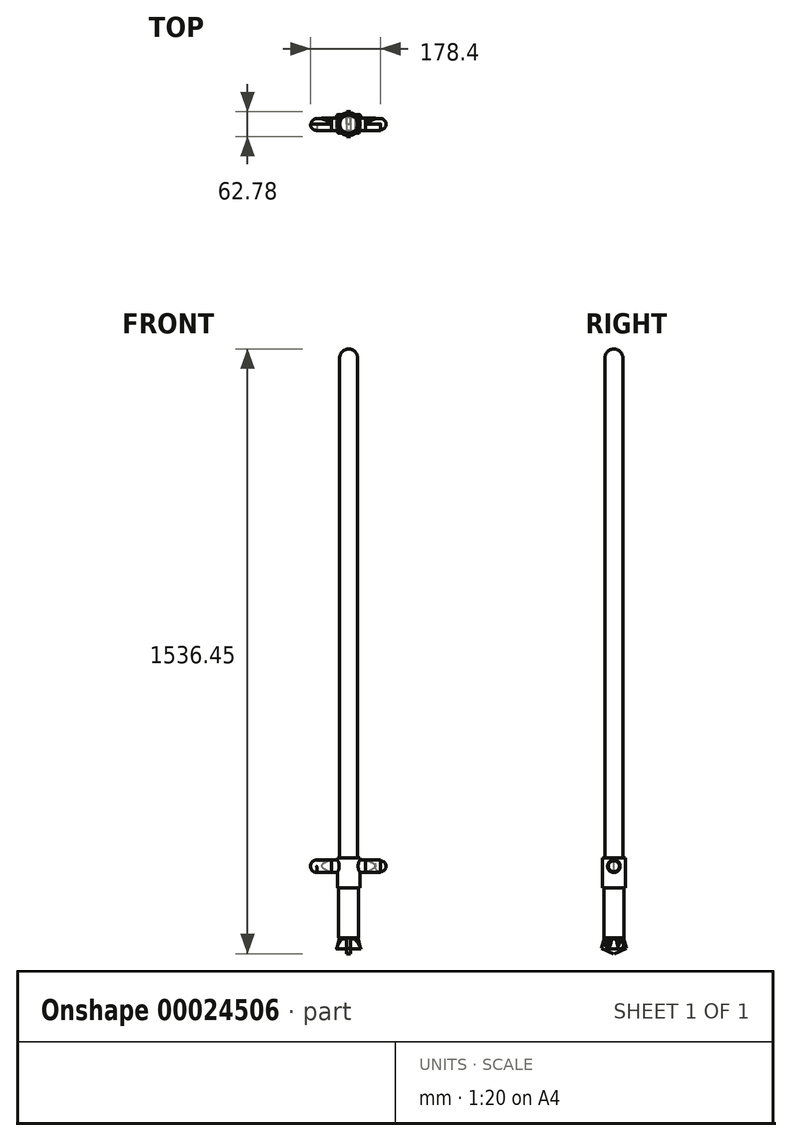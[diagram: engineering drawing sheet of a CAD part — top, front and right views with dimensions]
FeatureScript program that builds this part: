
annotation { "Feature Type Name" : "Feature", "Feature Type Description" : "" }
export const myFeature = defineFeature(function(context is Context, id is Id, definition is map)
    precondition{}
    {
        {
            var Q0;
            Q0=qCreatedBy(makeId("Top.planeOp"),FACE);
            var sketch = newSketch(context, id + "F0", { "sketchPlane" : qUnion([Q0])});
            skCircle(sketch, "E0", {"center": v(0, 0) * mm, "radius": 25.4 * mm});
            skSolve(sketch);
        }
        {
            var Q0;
            Q0 = qSketchRegion(id + "F0", true);
            extrude(context, id + "F1", {"entities" : qUnion([Q0]), "depth" : 152.4 * mm});
        }
        {
            var Q0;
            Q0=qCreatedBy(makeId("Right.planeOp"),FACE);
            var sketch = newSketch(context, id + "F2", { "sketchPlane" : qUnion([Q0])});
            skCircle(sketch, "E1", {"center": v(0, 131.2) * mm, "radius": 15.84 * mm});
            skSolve(sketch);
        }
        {
            var Q0;
            Q0 = qSketchRegion(id + "F2", true);
            extrude(context, id + "F3", {"entities" : qUnion([Q0]), "operationType" : NewBodyOperationType.ADD, "depth" : 43.18 * mm, "hasSecondDirection" : true, "secondDirectionOppositeDirection" : true, "secondDirectionDepth" : 43.18 * mm});
        }
        {
            var Q0;
            Q0=makeQuery(id+"F3.opExtrude","CAP_FACE",FACE,{"disambiguationData":[OSD([sQuery(id+"F2.wireOp",EDGE,"E1")])],"isStart":true});
            var sketch = newSketch(context, id + "F4", { "sketchPlane" : qUnion([Q0])});
            skArc(sketch, "E2", {"start": v(0, 147.04) * mm, "mid": v(-15.79, 131.2) * mm, "end": v(0, 115.37) * mm});
            skLineSegment(sketch, "E3", {"start": v(0, 147.04) * mm, "end": v(0, 145.08) * mm});
            skLineSegment(sketch, "E4", {"start": v(0, 115.37) * mm, "end": v(0, 117.32) * mm});
            skArc(sketch, "E5", {"start": v(0, 145.08) * mm, "mid": v(-14.08, 131.2) * mm, "end": v(0, 117.32) * mm});
            skSolve(sketch);
        }
        {
            var Q0;
            Q0 = qSketchRegion(id + "F4", true);
            extrude(context, id + "F5", {"entities" : qUnion([Q0]), "operationType" : NewBodyOperationType.ADD, "depth" : 25.4 * mm});
        }
        {
            var Q0;
            Q0=qCreatedBy(makeId("Front.planeOp"),FACE);
            cPlane(context, id + "F6", {"entities" : qUnion([Q0]), "cplaneType" : CPlaneType.OFFSET, "offset" : 25.4 * mm, "width" : 152.4 * mm, "height" : 152.4 * mm});
        }
        {
            var Q0;
            Q0=qCreatedBy(id+"F6.planeOp",FACE);
            var sketch = newSketch(context, id + "F7", { "sketchPlane" : qUnion([Q0])});
            skFitSpline(sketch, "E6", {"points": [v(-43.17, 147.15) * mm, v(-68.76, 132.35) * mm, v(-43.02, 115.24) * mm], "startDerivative": vector(-77.14, -28.96) * mm, "endDerivative": vector(76.87, -34.83) * mm});
            skLineSegment(sketch, "E7", {"start": v(-43.17, 147.15) * mm, "end": v(-43.17, 153) * mm});
            skLineSegment(sketch, "E8", {"start": v(-43.02, 115.24) * mm, "end": v(-43.02, 106.3) * mm});
            skLineSegment(sketch, "E9", {"start": v(-43.02, 106.3) * mm, "end": v(-74.3, 104.91) * mm});
            skLineSegment(sketch, "E10", {"start": v(-74.3, 104.91) * mm, "end": v(-72, 148.07) * mm});
            skLineSegment(sketch, "E11", {"start": v(-72, 148.07) * mm, "end": v(-43.17, 153) * mm});
            skSolve(sketch);
        }
        {
            var Q0;
            Q0 = qSketchRegion(id + "F7", true);
            extrude(context, id + "F8", {"entities" : qUnion([Q0]), "operationType" : NewBodyOperationType.REMOVE, "oppositeDirection" : true, "depth" : 50.68 * mm});
        }
        {
            var Q0;
            Q0=makeQuery(id+"F1.opExtrude","SWEPT_BODY",BODY,{"disambiguationData":[OSD([sQuery(id+"F0.wireOp",EDGE,"E0")])]});
            var Q1;
            Q1=qCreatedBy(makeId("Right.planeOp"),FACE);
            mirror(context, id + "F9", {"entities" : qUnion([Q0]), "mirrorPlane" : qUnion([Q1])});
        }
        {
            var Q0;
            Q0=makeQuery(id+"F1.opExtrude","CAP_FACE",FACE,{"disambiguationData":[OSD([sQuery(id+"F0.wireOp",EDGE,"E0")])],"isStart":false});
            var sketch = newSketch(context, id + "F10", { "sketchPlane" : qUnion([Q0])});
            skCircle(sketch, "E12", {"center": v(0, 0) * mm, "radius": 28.73 * mm});
            skSolve(sketch);
        }
        {
            var Q0;
            Q0=makeQuery(id+"F10.imprint","IMPRINT",FACE,{"disambiguationData":[TD([[makeQuery(id+"F10.imprint","IMPRINT",EDGE,{"derivedFrom":sQuery(id+"F10.wireOp",EDGE,"E12")}),1.0]])]});
            extrude(context, id + "F11", {"entities" : qUnion([Q0]), "operationType" : NewBodyOperationType.ADD, "oppositeDirection" : true, "depth" : 76.2 * mm});
        }
        {
            var Q0;
            Q0=makeQuery(id+"F1.opExtrude","CAP_FACE",FACE,{"disambiguationData":[OSD([sQuery(id+"F0.wireOp",EDGE,"E0")])],"isStart":true});
            extrude(context, id + "F12", {"entities" : qUnion([Q0]), "operationType" : NewBodyOperationType.ADD, "depth" : 50.8 * mm});
        }
        {
            var Q0;
            Q0=makeQuery(id+"F12.opExtrude","CAP_FACE",FACE,{"disambiguationData":[OSD([sQuery(id+"F0.wireOp",EDGE,"E0")])],"isStart":false});
            var sketch = newSketch(context, id + "F13", { "sketchPlane" : qUnion([Q0])});
            skLineSegment(sketch, "E13.bottom", {"start": v(-18.87, 17) * mm, "end": v(17.98, 17) * mm});
            skLineSegment(sketch, "E13.top", {"start": v(-18.87, -17.94) * mm, "end": v(17.98, -17.94) * mm});
            skLineSegment(sketch, "E13.left", {"start": v(-18.87, 17) * mm, "end": v(-18.87, -17.94) * mm});
            skLineSegment(sketch, "E13.right", {"start": v(17.98, 17) * mm, "end": v(17.98, -17.94) * mm});
            skSolve(sketch);
        }
        {
            var Q0;
            Q0 = qSketchRegion(id + "F13", true);
            extrude(context, id + "F14", {"entities" : qUnion([Q0]), "operationType" : NewBodyOperationType.ADD, "depth" : 2.54 * mm});
        }
        {
            var Q0;
            Q0=makeQuery(id+"F14.opExtrude","CAP_FACE",FACE,{"disambiguationData":[OSD([sQuery(id+"F13.wireOp",EDGE,"E13.bottom"),sQuery(id+"F13.wireOp",EDGE,"E13.top"),sQuery(id+"F13.wireOp",EDGE,"E13.left"),sQuery(id+"F13.wireOp",EDGE,"E13.right")])],"isStart":false});
            cPlane(context, id + "F15", {"entities" : qUnion([Q0]), "cplaneType" : CPlaneType.OFFSET, "offset" : 25.4 * mm, "width" : 152.4 * mm, "height" : 152.4 * mm});
        }
        {
            var Q0;
            Q0=qCreatedBy(id+"F15.planeOp",FACE);
            var sketch = newSketch(context, id + "F16", { "sketchPlane" : qUnion([Q0])});
            skLineSegment(sketch, "E14.bottom", {"start": v(-31.75, 31.75) * mm, "end": v(31.75, 31.75) * mm});
            skLineSegment(sketch, "E14.top", {"start": v(-31.75, -31.75) * mm, "end": v(31.75, -31.75) * mm});
            skLineSegment(sketch, "E14.left", {"start": v(-31.75, 31.75) * mm, "end": v(-31.75, -31.75) * mm});
            skLineSegment(sketch, "E14.right", {"start": v(31.75, 31.75) * mm, "end": v(31.75, -31.75) * mm});
            skSolve(sketch);
        }
        {
            var Q1;
            Q1=makeQuery(id+"F14.opExtrude","CAP_FACE",FACE,{"disambiguationData":[OSD([sQuery(id+"F13.wireOp",EDGE,"E13.bottom"),sQuery(id+"F13.wireOp",EDGE,"E13.top"),sQuery(id+"F13.wireOp",EDGE,"E13.left"),sQuery(id+"F13.wireOp",EDGE,"E13.right")])],"isStart":false});
            var Q2;
            Q2=makeQuery(id+"F16.imprint","IMPRINT",FACE,{"disambiguationData":[TD([[makeQuery(id+"F16.imprint","IMPRINT",EDGE,{"derivedFrom":sQuery(id+"F16.wireOp",EDGE,"E14.bottom")}),-1.0]])]});
            loft(context, id + "F17", {"operationType" : NewBodyOperationType.ADD, "sheetProfilesArray" : [{ "sheetProfileEntities" : qUnion([Q1]) }, { "sheetProfileEntities" : qUnion([Q2]) }]});
        }
        {
            var Q0;
            Q0=makeQuery(id+"F17.opLoft","CAP_FACE",FACE,{"disambiguationData":[OSD([makeQuery(id+"F16.imprint","IMPRINT",FACE,{"disambiguationData":[TD([[makeQuery(id+"F16.imprint","IMPRINT",EDGE,{"derivedFrom":sQuery(id+"F16.wireOp",EDGE,"E14.bottom")}),-1.0]])]})])],"isStart":true});
            var sketch = newSketch(context, id + "F18", { "sketchPlane" : qUnion([Q0])});
            skCircle(sketch, "E15", {"center": v(0, 0) * mm, "radius": 23.24 * mm});
            skSolve(sketch);
        }
        {
            var Q0;
            Q0=qCreatedBy(makeId("Right.planeOp"),FACE);
            var sketch = newSketch(context, id + "F19", { "sketchPlane" : qUnion([Q0])});
            skLineSegment(sketch, "E16", {"start": v(-15.1, -41.8) * mm, "end": v(-31.4, -77.47) * mm});
            skLineSegment(sketch, "E17", {"start": v(-15.1, -41.8) * mm, "end": v(-21, -39.1) * mm});
            skLineSegment(sketch, "E18", {"start": v(-21, -39.1) * mm, "end": v(-31.4, -77.47) * mm});
            skSolve(sketch);
        }
        {
            var Q0;
            Q0 = qSketchRegion(id + "F19", true);
            extrude(context, id + "F20", {"entities" : qUnion([Q0]), "depth" : 5.08 * mm, "hasSecondDirection" : true, "secondDirectionOppositeDirection" : true, "secondDirectionDepth" : 5.08 * mm});
        }
        {
            var Q0;
            Q0=makeQuery(id+"F20.opExtrude","SWEPT_BODY",BODY,{"disambiguationData":[OSD([sQuery(id+"F19.wireOp",EDGE,"E16"),sQuery(id+"F19.wireOp",EDGE,"E17"),sQuery(id+"F19.wireOp",EDGE,"E18")])]});
            var Q1;
            Q1=sQuery(id+"F18.wireOp",EDGE,"E15");
            circularPattern(context, id + "F21", {"operationType" : NewBodyOperationType.ADD, "entities" : qUnion([Q0]), "axis" : qUnion([Q1]), "angle" : 60 * degree, "instanceCount" : 6});
        }
        {
            var Q0;
            Q0=makeQuery(id+"F17.opLoft","MID_CAP_EDGE",EDGE,{"disambiguationData":[OSD([sQuery(id+"F16.wireOp",EDGE,"E14.bottom"),sQuery(id+"F16.wireOp",EDGE,"E14.left"),sQuery(id+"F16.wireOp",EDGE,"E14.right")])],"capPos":1.0});
            fillet(context, id + "F22", {"entities" : qUnion([Q0]), "radius" : 12.7 * mm, "tangentPropagation" : true, "allowEdgeOverflow" : false});
        }
        {
            var Q0;
            Q0=makeQuery(id+"F17.opLoft","MID_CAP_EDGE",EDGE,{"disambiguationData":[OSD([sQuery(id+"F16.wireOp",EDGE,"E14.top"),sQuery(id+"F16.wireOp",EDGE,"E14.left"),sQuery(id+"F16.wireOp",EDGE,"E14.right")])],"capPos":1.0});
            fillet(context, id + "F23", {"entities" : qUnion([Q0]), "radius" : 10.16 * mm, "tangentPropagation" : true, "allowEdgeOverflow" : false});
        }
        {
            var Q0;
            Q0=makeQuery(id+"F21.opPattern","COPY",FACE,{"derivedFrom":makeQuery(id+"F20.opExtrude","SWEPT_FACE",FACE,{"disambiguationData":[OSD([sQuery(id+"F19.wireOp",EDGE,"E16")])]}),"instanceName":"3"});
            extrude(context, id + "F24", {"entities" : qUnion([Q0]), "operationType" : NewBodyOperationType.ADD, "depth" : 33.02 * mm});
        }
        {
            var Q0;
            Q0=makeQuery(id+"F20.opExtrude","SWEPT_FACE",FACE,{"disambiguationData":[OSD([sQuery(id+"F19.wireOp",EDGE,"E16")])]});
            extrude(context, id + "F25", {"entities" : qUnion([Q0]), "operationType" : NewBodyOperationType.ADD, "depth" : 33.02 * mm});
        }
        {
            var Q0;
            {var subQ0=sQuery(id+"F0.wireOp",EDGE,"E0");var subQ1=makeQuery(id+"F1.opExtrude","CAP_FACE",FACE,{"disambiguationData":[OSD([subQ0])],"isStart":false});Q0=makeQuery(id+"F11.boolean.opBoolean","MERGE",FACE,{"derivedFrom":[subQ1,makeQuery(id+"F9.opPattern","COPY",FACE,{"derivedFrom":subQ1,"instanceName":"1"}),makeQuery(id+"F11.opExtrude","CAP_FACE",FACE,{"disambiguationData":[OSD([subQ0,sQuery(id+"F10.wireOp",EDGE,"E12")])],"isStart":true})]});}
            var sketch = newSketch(context, id + "F26", { "sketchPlane" : qUnion([Q0])});
            skCircle(sketch, "E19", {"center": v(0, 0) * mm, "radius": 22.86 * mm});
            skSolve(sketch);
        }
        {
            var Q0;
            Q0 = qSketchRegion(id + "F26", true);
            extrude(context, id + "F27", {"entities" : qUnion([Q0]), "depth" : 1270 * mm});
        }
        {
            var Q0;
            {var subQ0=sQuery(id+"F2.wireOp",EDGE,"E1");var subQ1=makeQuery(id+"F3.opExtrude","CAP_FACE",FACE,{"disambiguationData":[OSD([subQ0])],"isStart":false});Q0=makeQuery(id+"F11.boolean.opBoolean","SPLIT",FACE,{"disambiguationData":[TD([makeQuery(id+"F3.opExtrude","SWEPT_FACE",FACE,{"disambiguationData":[OSD([subQ0])]}),subQ1,makeQuery(id+"F9.opPattern","COPY",FACE,{"derivedFrom":makeQuery(id+"F5.opExtrude","SWEPT_FACE",FACE,{"disambiguationData":[OSD([sQuery(id+"F4.wireOp",EDGE,"E2")])]}),"instanceName":"1"}),makeQuery(id+"F9.opPattern","COPY",FACE,{"derivedFrom":makeQuery(id+"F5.opExtrude","SWEPT_FACE",FACE,{"disambiguationData":[OSD([sQuery(id+"F4.wireOp",EDGE,"E3")])]}),"instanceName":"1"}),makeQuery(id+"F9.opPattern","COPY",FACE,{"derivedFrom":makeQuery(id+"F5.opExtrude","SWEPT_FACE",FACE,{"disambiguationData":[OSD([sQuery(id+"F4.wireOp",EDGE,"E4")])]}),"instanceName":"1"}),makeQuery(id+"F9.opPattern","COPY",FACE,{"derivedFrom":makeQuery(id+"F5.opExtrude","SWEPT_FACE",FACE,{"disambiguationData":[OSD([sQuery(id+"F4.wireOp",EDGE,"E5")])]}),"instanceName":"1"})])],"derivedFrom":subQ1});}
            extrude(context, id + "F28", {"entities" : qUnion([Q0]), "depth" : 38.1 * mm});
        }
        {
            var Q0;
            {var subQ0=sQuery(id+"F2.wireOp",EDGE,"E1");var subQ1=makeQuery(id+"F3.opExtrude","CAP_FACE",FACE,{"disambiguationData":[OSD([subQ0])],"isStart":true});Q0=makeQuery(id+"F5.boolean.opBoolean","SPLIT",FACE,{"disambiguationData":[TD([makeQuery(id+"F3.opExtrude","SWEPT_FACE",FACE,{"disambiguationData":[OSD([subQ0])]}),subQ1,makeQuery(id+"F5.opExtrude","SWEPT_FACE",FACE,{"disambiguationData":[OSD([sQuery(id+"F4.wireOp",EDGE,"E2")])]}),makeQuery(id+"F5.opExtrude","SWEPT_FACE",FACE,{"disambiguationData":[OSD([sQuery(id+"F4.wireOp",EDGE,"E3")])]}),makeQuery(id+"F5.opExtrude","SWEPT_FACE",FACE,{"disambiguationData":[OSD([sQuery(id+"F4.wireOp",EDGE,"E4")])]}),makeQuery(id+"F5.opExtrude","SWEPT_FACE",FACE,{"disambiguationData":[OSD([sQuery(id+"F4.wireOp",EDGE,"E5")])]})])],"derivedFrom":subQ1});}
            extrude(context, id + "F29", {"entities" : qUnion([Q0]), "depth" : 38.1 * mm});
        }
        {
            var Q0;
            Q0=makeQuery(id+"F29.opExtrude","CAP_FACE",FACE,{"disambiguationData":[OSD([sQuery(id+"F2.wireOp",EDGE,"E1")])],"isStart":false});
            var sketch = newSketch(context, id + "F30", { "sketchPlane" : qUnion([Q0])});
            skLineSegment(sketch, "E20", {"start": v(-14.08, 131.2) * mm, "end": v(15.84, 131.2) * mm});
            skSolve(sketch);
        }
        {
            var Q0;
            Q0 = qSketchRegion(id + "F30", true);
            var Q1;
            {var subQ0=sQuery(id+"F30.wireOp",EDGE,"E20");Q1=makeQuery(id+"F30.imprint","IMPRINT",FACE,{"disambiguationData":[TD([[makeQuery(id+"F30.imprint","IMPRINT",EDGE,{"derivedFrom":subQ0}),1.0]])]});}
            var Q2;
            Q2=sQuery(id+"F30.wireOp",EDGE,"E20");
            revolve(context, id + "F31", {"operationType" : NewBodyOperationType.ADD, "entities" : qUnion([Q0, Q1]), "axis" : qUnion([Q2]), "revolveType" : RevolveType.FULL});
        }
        {
            var Q0;
            Q0=makeQuery(id+"F28.opExtrude","CAP_FACE",FACE,{"disambiguationData":[OSD([sQuery(id+"F2.wireOp",EDGE,"E1")])],"isStart":false});
            var sketch = newSketch(context, id + "F32", { "sketchPlane" : qUnion([Q0])});
            skLineSegment(sketch, "E21", {"start": v(0, 147.04) * mm, "end": v(0, 115.37) * mm});
            skSolve(sketch);
        }
        {
            var Q0;
            {var subQ1=makeQuery(id+"F28.opExtrude","CAP_EDGE",EDGE,{"disambiguationData":[OSD([sQuery(id+"F4.wireOp",EDGE,"E5")])],"isStart":false});Q0=makeQuery(id+"F32.imprint","IMPRINT",FACE,{"disambiguationData":[TD([[makeQuery(id+"F32.imprint","IMPRINT",EDGE,{"derivedFrom":subQ1}),-1.0]])]});}
            var Q1;
            Q1=sQuery(id+"F32.wireOp",EDGE,"E21");
            revolve(context, id + "F33", {"operationType" : NewBodyOperationType.ADD, "entities" : qUnion([Q0]), "axis" : qUnion([Q1]), "revolveType" : RevolveType.FULL});
        }
        {
            var Q0;
            Q0=makeQuery(id+"F27.opExtrude","CAP_FACE",FACE,{"disambiguationData":[OSD([sQuery(id+"F26.wireOp",EDGE,"E19")])],"isStart":false});
            var sketch = newSketch(context, id + "F34", { "sketchPlane" : qUnion([Q0])});
            skLineSegment(sketch, "E22", {"start": v(22.86, 0) * mm, "end": v(-22.86, 0) * mm});
            skSolve(sketch);
        }
        {
            var Q0;
            {var subQ0=sQuery(id+"F34.wireOp",EDGE,"E22");Q0=makeQuery(id+"F34.imprint","IMPRINT",FACE,{"disambiguationData":[TD([[makeQuery(id+"F34.imprint","IMPRINT",EDGE,{"derivedFrom":subQ0}),1.0]])]});}
            var Q1;
            Q1=sQuery(id+"F34.wireOp",EDGE,"E22");
            revolve(context, id + "F35", {"operationType" : NewBodyOperationType.ADD, "entities" : qUnion([Q0]), "axis" : qUnion([Q1]), "revolveType" : RevolveType.FULL});
        }
    });
